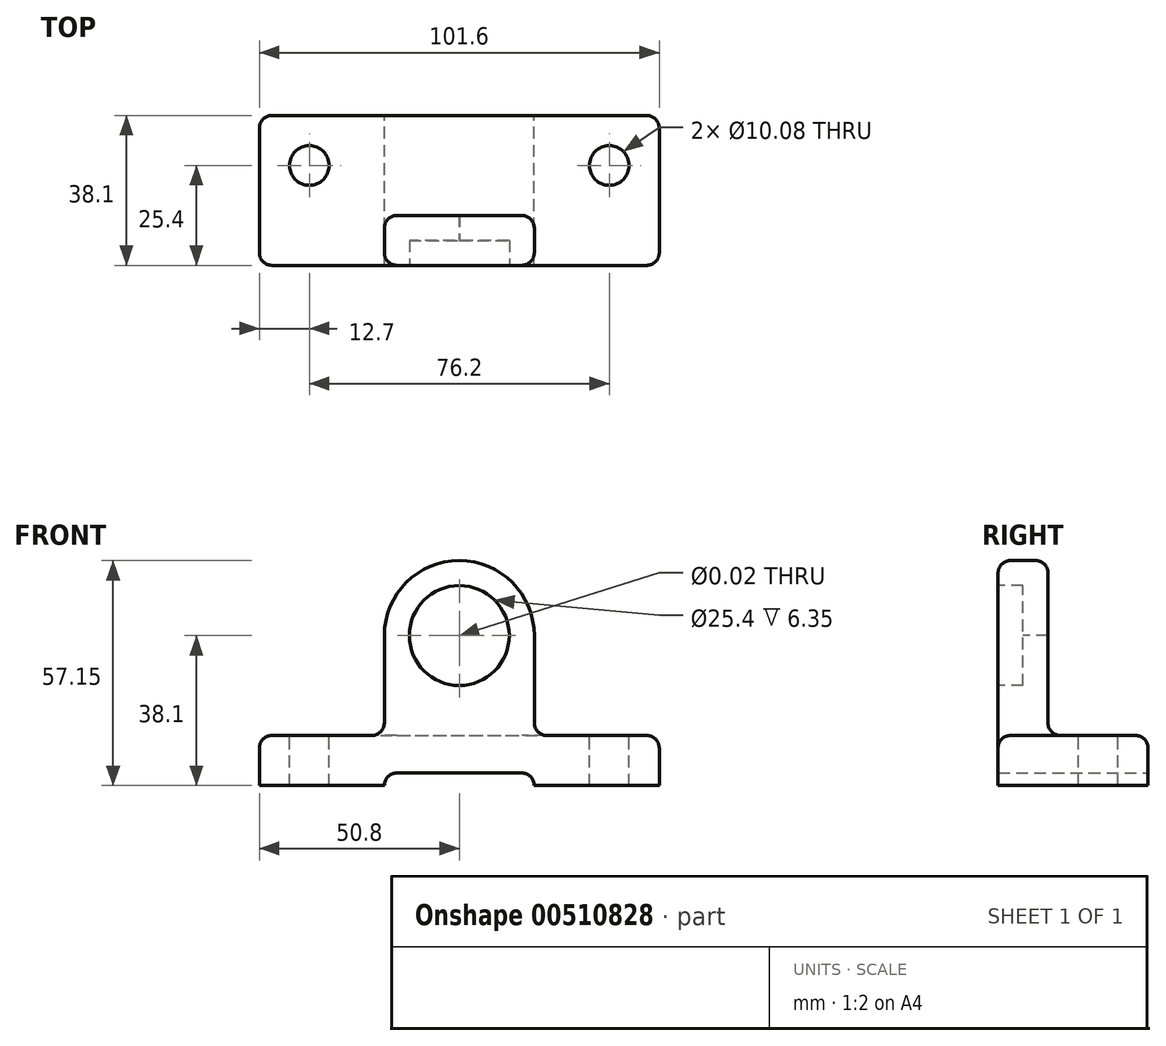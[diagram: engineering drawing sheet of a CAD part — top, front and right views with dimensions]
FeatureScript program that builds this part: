
annotation { "Feature Type Name" : "Feature", "Feature Type Description" : "" }
export const myFeature = defineFeature(function(context is Context, id is Id, definition is map)
    precondition{}
    {
        {
            var Q0;
            Q0=qCreatedBy(makeId("Top.planeOp"),FACE);
            var sketch = newSketch(context, id + "F0", { "sketchPlane" : qUnion([Q0])});
            skLineSegment(sketch, "E0.bottom", {"start": v(0, 0) * mm, "end": v(101.6, 0) * mm});
            skLineSegment(sketch, "E0.top", {"start": v(0, 38.1) * mm, "end": v(101.6, 38.1) * mm});
            skLineSegment(sketch, "E0.left", {"start": v(0, 0) * mm, "end": v(0, 38.1) * mm});
            skLineSegment(sketch, "E0.right", {"start": v(101.6, 0) * mm, "end": v(101.6, 38.1) * mm});
            skSolve(sketch);
        }
        {
            var Q0;
            Q0 = qSketchRegion(id + "F0", true);
            extrude(context, id + "F1", {"entities" : qUnion([Q0]), "depth" : 12.7 * mm, "offsetDistance" : 25.4 * mm});
        }
        {
            var Q0;
            Q0=makeQuery(id+"F1.opExtrude","SWEPT_FACE",FACE,{"disambiguationData":[OSD([sQuery(id+"F0.wireOp",EDGE,"E0.bottom")])]});
            var sketch = newSketch(context, id + "F2", { "sketchPlane" : qUnion([Q0])});
            skLineSegment(sketch, "E1", {"start": v(31.75, 0) * mm, "end": v(31.75, 38.1) * mm});
            skArc(sketch, "E2", {"start": v(69.85, 38.1) * mm, "mid": v(50.8, 57.15) * mm, "end": v(31.75, 38.1) * mm});
            skLineSegment(sketch, "E3", {"start": v(69.85, 38.1) * mm, "end": v(69.85, 0) * mm});
            skSolve(sketch);
        }
        {
            var Q0;
            {var subQ0=sQuery(id+"F2.wireOp",EDGE,"E2");Q0=makeQuery(id+"F2.imprint","IMPRINT",FACE,{"disambiguationData":[TD([[makeQuery(id+"F2.imprint","IMPRINT",EDGE,{"derivedFrom":subQ0}),1.0]])]});}
            var Q1;
            {var subQ0=sQuery(id+"F2.wireOp",EDGE,"E1");var subQ1=sQuery(id+"F0.wireOp",EDGE,"E0.bottom");var subQ2=makeQuery(id+"F1.opExtrude","CAP_EDGE",EDGE,{"disambiguationData":[OSD([subQ1])],"isStart":true});var subQ3=makeQuery(id+"F2.imprint","INTERSECT",VERTEX,{"derivedFrom":[subQ2,subQ0]});Q1=makeQuery(id+"F2.imprint","IMPRINT",FACE,{"disambiguationData":[TD([[makeQuery(id+"F2.imprint","IMPRINT",EDGE,{"disambiguationData":[TD([[subQ3,-1.0]])],"derivedFrom":subQ0}),-1.0]])]});}
            extrude(context, id + "F3", {"entities" : qUnion([Q0, Q1]), "operationType" : NewBodyOperationType.ADD, "oppositeDirection" : true, "depth" : 12.7 * mm, "offsetDistance" : 25.4 * mm});
        }
        {
            var Q0;
            Q0=sQuery(id+"F2.wireOp",VERTEX,"E2.center");
            var Q1;
            Q1=makeQuery(id+"F1.opExtrude","SWEPT_BODY",BODY,{"disambiguationData":[OSD([sQuery(id+"F0.wireOp",EDGE,"E0.bottom"),sQuery(id+"F0.wireOp",EDGE,"E0.top"),sQuery(id+"F0.wireOp",EDGE,"E0.left"),sQuery(id+"F0.wireOp",EDGE,"E0.right")])]});
            hole(context, id + "F4", {"style" : HoleStyle.C_BORE, "endStyle" : HoleEndStyle.THROUGH, "standardTappedOrClearance" : lookupTablePath({ "standard" : "ANSI", "size" : "15/32 (0.47)", "type" : "Drilled" }), "standardBlindInLast" : lookupTablePath({ "standard" : "ANSI", "size" : "15/32", "type" : "Drilled" }), "holeDiameter" : 15 / 812.8 * mm, "cBoreDiameter" : 25.4 * mm, "cBoreDepth" : 6.35 * mm, "isTappedThrough" : true, "tappedDepth" : 12.7 * mm, "tapClearance" : 3, "locations" : qUnion([Q0]), "scope" : qUnion([Q1])});
        }
        {
            var Q0;
            Q0=makeQuery(id+"F1.opExtrude","SWEPT_FACE",FACE,{"disambiguationData":[OSD([sQuery(id+"F0.wireOp",EDGE,"E0.top")])]});
            var sketch = newSketch(context, id + "F5", { "sketchPlane" : qUnion([Q0])});
            skLineSegment(sketch, "E4", {"start": v(-69.83, 0) * mm, "end": v(-69.83, 3.17) * mm});
            skLineSegment(sketch, "E5", {"start": v(-31.77, 3.18) * mm, "end": v(-31.77, 0) * mm});
            skLineSegment(sketch, "E6", {"start": v(-69.83, 3.17) * mm, "end": v(-31.77, 3.18) * mm});
            skLineSegment(sketch, "E7", {"start": v(-69.83, 0) * mm, "end": v(-31.77, 0) * mm});
            skSolve(sketch);
        }
        {
            var Q0;
            Q0=makeQuery(id+"F5.imprint","IMPRINT",FACE,{"disambiguationData":[TD([[makeQuery(id+"F5.imprint","IMPRINT",EDGE,{"derivedFrom":sQuery(id+"F5.wireOp",EDGE,"E4")}),-1.0]])]});
            extrude(context, id + "F6", {"entities" : qUnion([Q0]), "operationType" : NewBodyOperationType.REMOVE, "endBound" : BoundingType.THROUGH_ALL, "oppositeDirection" : true, "depth" : 25.4 * mm});
        }
        {
            var Q0;
            Q0=makeQuery(id+"F1.opExtrude","CAP_FACE",FACE,{"disambiguationData":[OSD([sQuery(id+"F0.wireOp",EDGE,"E0.bottom"),sQuery(id+"F0.wireOp",EDGE,"E0.top"),sQuery(id+"F0.wireOp",EDGE,"E0.left"),sQuery(id+"F0.wireOp",EDGE,"E0.right")])],"isStart":false});
            var sketch = newSketch(context, id + "F7", { "sketchPlane" : qUnion([Q0])});
            skPoint(sketch, "E8", {"position": v(12.7, 25.4) * mm});
            skPoint(sketch, "E9", {"position": v(88.9, 25.4) * mm});
            skSolve(sketch);
        }
        {
            var Q0;
            Q0=sQuery(id+"F7.wireOp",VERTEX,"E8");
            var Q1;
            Q1=sQuery(id+"F7.wireOp",VERTEX,"E9");
            var Q2;
            Q2=makeQuery(id+"F1.opExtrude","SWEPT_BODY",BODY,{"disambiguationData":[OSD([sQuery(id+"F0.wireOp",EDGE,"E0.bottom"),sQuery(id+"F0.wireOp",EDGE,"E0.top"),sQuery(id+"F0.wireOp",EDGE,"E0.left"),sQuery(id+"F0.wireOp",EDGE,"E0.right")])]});
            hole(context, id + "F8", {"style" : HoleStyle.SIMPLE, "endStyle" : HoleEndStyle.THROUGH, "standardTappedOrClearance" : lookupTablePath({ "standard" : "ANSI", "fit" : "Normal (ASME)", "size" : "3/8", "type" : "Clearance" }), "standardBlindInLast" : lookupTablePath({ "fit" : "Free", "standard" : "ANSI", "size" : "3/8", "type" : "Clearance" }), "holeDiameter" : 10.08 * mm, "isTappedThrough" : true, "tappedDepth" : 12.7 * mm, "tapClearance" : 3, "locations" : qUnion([Q0, Q1]), "scope" : qUnion([Q2])});
        }
        {
            var Q0;
            Q0=makeQuery(id+"F1.opExtrude","SWEPT_EDGE",EDGE,{"disambiguationData":[OSD([sQuery(id+"F0.wireOp",EDGE,"E0.top"),sQuery(id+"F0.wireOp",EDGE,"E0.right")])]});
            var Q1;
            Q1=makeQuery(id+"F1.opExtrude","SWEPT_EDGE",EDGE,{"disambiguationData":[OSD([sQuery(id+"F0.wireOp",EDGE,"E0.top"),sQuery(id+"F0.wireOp",EDGE,"E0.left")])]});
            var Q2;
            Q2=makeQuery(id+"F1.opExtrude","SWEPT_EDGE",EDGE,{"disambiguationData":[OSD([sQuery(id+"F0.wireOp",EDGE,"E0.bottom"),sQuery(id+"F0.wireOp",EDGE,"E0.left")])]});
            var Q3;
            Q3=makeQuery(id+"F1.opExtrude","SWEPT_EDGE",EDGE,{"disambiguationData":[OSD([sQuery(id+"F0.wireOp",EDGE,"E0.bottom"),sQuery(id+"F0.wireOp",EDGE,"E0.right")])]});
            var Q4;
            Q4=makeQuery(id+"F6.boolean.opBoolean","COPY",EDGE,{"derivedFrom":makeQuery(id+"F6.opExtrude","SWEPT_EDGE",EDGE,{"disambiguationData":[OSD([sQuery(id+"F5.wireOp",EDGE,"E5"),sQuery(id+"F5.wireOp",EDGE,"E6")])]})});
            var Q5;
            Q5=makeQuery(id+"F6.boolean.opBoolean","COPY",EDGE,{"derivedFrom":makeQuery(id+"F6.opExtrude","SWEPT_EDGE",EDGE,{"disambiguationData":[OSD([sQuery(id+"F5.wireOp",EDGE,"E4"),sQuery(id+"F5.wireOp",EDGE,"E6")])]})});
            fillet(context, id + "F9", {"entities" : qUnion([Q0, Q1, Q2, Q3, Q4, Q5]), "radius" : 3.17 * mm, "tangentPropagation" : true, "allowEdgeOverflow" : false});
        }
        {
            var Q0;
            {var subQ1=sQuery(id+"F0.wireOp",EDGE,"E0.left");var subQ2=sQuery(id+"F0.wireOp",EDGE,"E0.bottom");Q0=makeQuery(id+"F3.boolean.opBoolean","SPLIT",EDGE,{"disambiguationData":[TD([makeQuery(id+"F1.opExtrude","SWEPT_FACE",FACE,{"disambiguationData":[OSD([subQ1])]})])],"derivedFrom":makeQuery(id+"F1.opExtrude","CAP_EDGE",EDGE,{"disambiguationData":[OSD([subQ2])],"isStart":false})});}
            var Q1;
            Q1=makeQuery(id+"F1.opExtrude","CAP_EDGE",EDGE,{"disambiguationData":[OSD([sQuery(id+"F0.wireOp",EDGE,"E0.top")])],"isStart":false});
            var Q2;
            Q2=makeQuery(id+"F1.opExtrude","CAP_EDGE",EDGE,{"disambiguationData":[OSD([sQuery(id+"F0.wireOp",EDGE,"E0.left")])],"isStart":false});
            var Q3;
            {var subQ1=sQuery(id+"F0.wireOp",EDGE,"E0.bottom");var subQ2=sQuery(id+"F0.wireOp",EDGE,"E0.right");Q3=makeQuery(id+"F3.boolean.opBoolean","SPLIT",EDGE,{"disambiguationData":[TD([makeQuery(id+"F1.opExtrude","SWEPT_FACE",FACE,{"disambiguationData":[OSD([subQ2])]})])],"derivedFrom":makeQuery(id+"F1.opExtrude","CAP_EDGE",EDGE,{"disambiguationData":[OSD([subQ1])],"isStart":false})});}
            var Q4;
            Q4=makeQuery(id+"F1.opExtrude","CAP_EDGE",EDGE,{"disambiguationData":[OSD([sQuery(id+"F0.wireOp",EDGE,"E0.right")])],"isStart":false});
            var Q5;
            Q5=makeQuery(id+"F3.boolean.opBoolean","INTERSECT",EDGE,{"derivedFrom":[makeQuery(id+"F1.opExtrude","CAP_FACE",FACE,{"disambiguationData":[OSD([sQuery(id+"F0.wireOp",EDGE,"E0.bottom"),sQuery(id+"F0.wireOp",EDGE,"E0.top"),sQuery(id+"F0.wireOp",EDGE,"E0.left"),sQuery(id+"F0.wireOp",EDGE,"E0.right")])],"isStart":false}),makeQuery(id+"F3.opExtrude","SWEPT_FACE",FACE,{"disambiguationData":[OSD([sQuery(id+"F2.wireOp",EDGE,"E3")])]})]});
            var Q6;
            Q6=makeQuery(id+"F3.opExtrude","CAP_EDGE",EDGE,{"disambiguationData":[OSD([sQuery(id+"F2.wireOp",EDGE,"E2")])],"isStart":true});
            var Q7;
            Q7=makeQuery(id+"F3.opExtrude","CAP_EDGE",EDGE,{"disambiguationData":[OSD([sQuery(id+"F2.wireOp",EDGE,"E2")])],"isStart":false});
            var Q8;
            Q8=makeQuery(id+"F3.opExtrude","CAP_EDGE",EDGE,{"disambiguationData":[OSD([sQuery(id+"F2.wireOp",EDGE,"E3")])],"isStart":false});
            var Q9;
            {var subQ0=sQuery(id+"F0.wireOp",EDGE,"E0.bottom");Q9=makeQuery(id+"F3.boolean.opBoolean","INTERSECT",EDGE,{"derivedFrom":[makeQuery(id+"F1.opExtrude","CAP_FACE",FACE,{"disambiguationData":[OSD([subQ0,sQuery(id+"F0.wireOp",EDGE,"E0.top"),sQuery(id+"F0.wireOp",EDGE,"E0.left"),sQuery(id+"F0.wireOp",EDGE,"E0.right")])],"isStart":false}),makeQuery(id+"F3.opExtrude","CAP_FACE",FACE,{"disambiguationData":[OSD([subQ0,sQuery(id+"F2.wireOp",EDGE,"E1"),sQuery(id+"F2.wireOp",EDGE,"E2"),sQuery(id+"F2.wireOp",EDGE,"E3")])],"isStart":false})]});}
            var Q10;
            Q10=makeQuery(id+"F3.boolean.opBoolean","INTERSECT",EDGE,{"derivedFrom":[makeQuery(id+"F1.opExtrude","CAP_FACE",FACE,{"disambiguationData":[OSD([sQuery(id+"F0.wireOp",EDGE,"E0.bottom"),sQuery(id+"F0.wireOp",EDGE,"E0.top"),sQuery(id+"F0.wireOp",EDGE,"E0.left"),sQuery(id+"F0.wireOp",EDGE,"E0.right")])],"isStart":false}),makeQuery(id+"F3.opExtrude","SWEPT_FACE",FACE,{"disambiguationData":[OSD([sQuery(id+"F2.wireOp",EDGE,"E1")])]})]});
            var Q11;
            Q11=makeQuery(id+"F3.opExtrude","CAP_EDGE",EDGE,{"disambiguationData":[OSD([sQuery(id+"F2.wireOp",EDGE,"E1")])],"isStart":false});
            var Q12;
            Q12=makeQuery(id+"F3.opExtrude","CAP_EDGE",EDGE,{"disambiguationData":[OSD([sQuery(id+"F2.wireOp",EDGE,"E1")])],"isStart":true});
            var Q13;
            Q13=makeQuery(id+"F3.opExtrude","CAP_EDGE",EDGE,{"disambiguationData":[OSD([sQuery(id+"F2.wireOp",EDGE,"E3")])],"isStart":true});
            fillet(context, id + "F10", {"entities" : qUnion([Q0, Q1, Q2, Q3, Q4, Q5, Q6, Q7, Q8, Q9, Q10, Q11, Q12, Q13]), "radius" : 3.17 * mm, "tangentPropagation" : true, "allowEdgeOverflow" : false});
        }
    });
